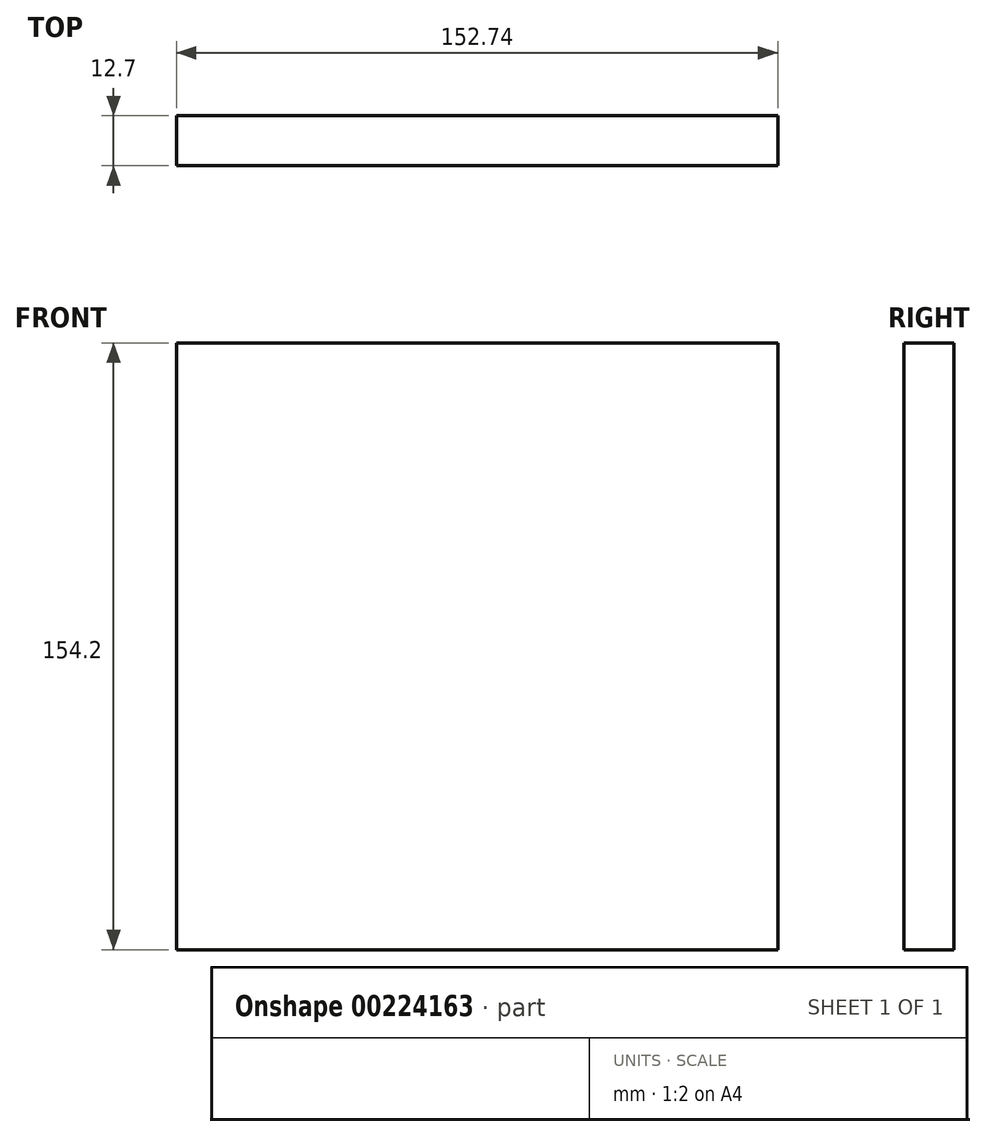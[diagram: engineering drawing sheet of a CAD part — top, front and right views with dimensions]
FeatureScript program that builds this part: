
annotation { "Feature Type Name" : "Feature", "Feature Type Description" : "" }
export const myFeature = defineFeature(function(context is Context, id is Id, definition is map)
    precondition{}
    {
        {
            var Q0;
            Q0=qCreatedBy(makeId("Front.planeOp"),FACE);
            var sketch = newSketch(context, id + "F0", { "sketchPlane" : qUnion([Q0])});
            skLineSegment(sketch, "E0.bottom", {"start": v(-76.37, 77.1) * mm, "end": v(76.37, 77.1) * mm});
            skLineSegment(sketch, "E0.top", {"start": v(-76.37, -77.1) * mm, "end": v(76.37, -77.1) * mm});
            skLineSegment(sketch, "E0.left", {"start": v(-76.37, 77.1) * mm, "end": v(-76.37, -77.1) * mm});
            skLineSegment(sketch, "E0.right", {"start": v(76.37, 77.1) * mm, "end": v(76.37, -77.1) * mm});
            skPoint(sketch, "E0.middle", {"position": v(0, 0) * mm});
            skSolve(sketch);
        }
        {
            var Q0;
            Q0=makeQuery(id+"F0.imprint","IMPRINT",FACE,{"disambiguationData":[TD([[makeQuery(id+"F0.imprint","IMPRINT",EDGE,{"derivedFrom":sQuery(id+"F0.wireOp",EDGE,"E0.bottom")}),-1.0]])]});
            extrude(context, id + "F1", {"entities" : qUnion([Q0]), "depth" : 12.7 * mm});
        }
    });
